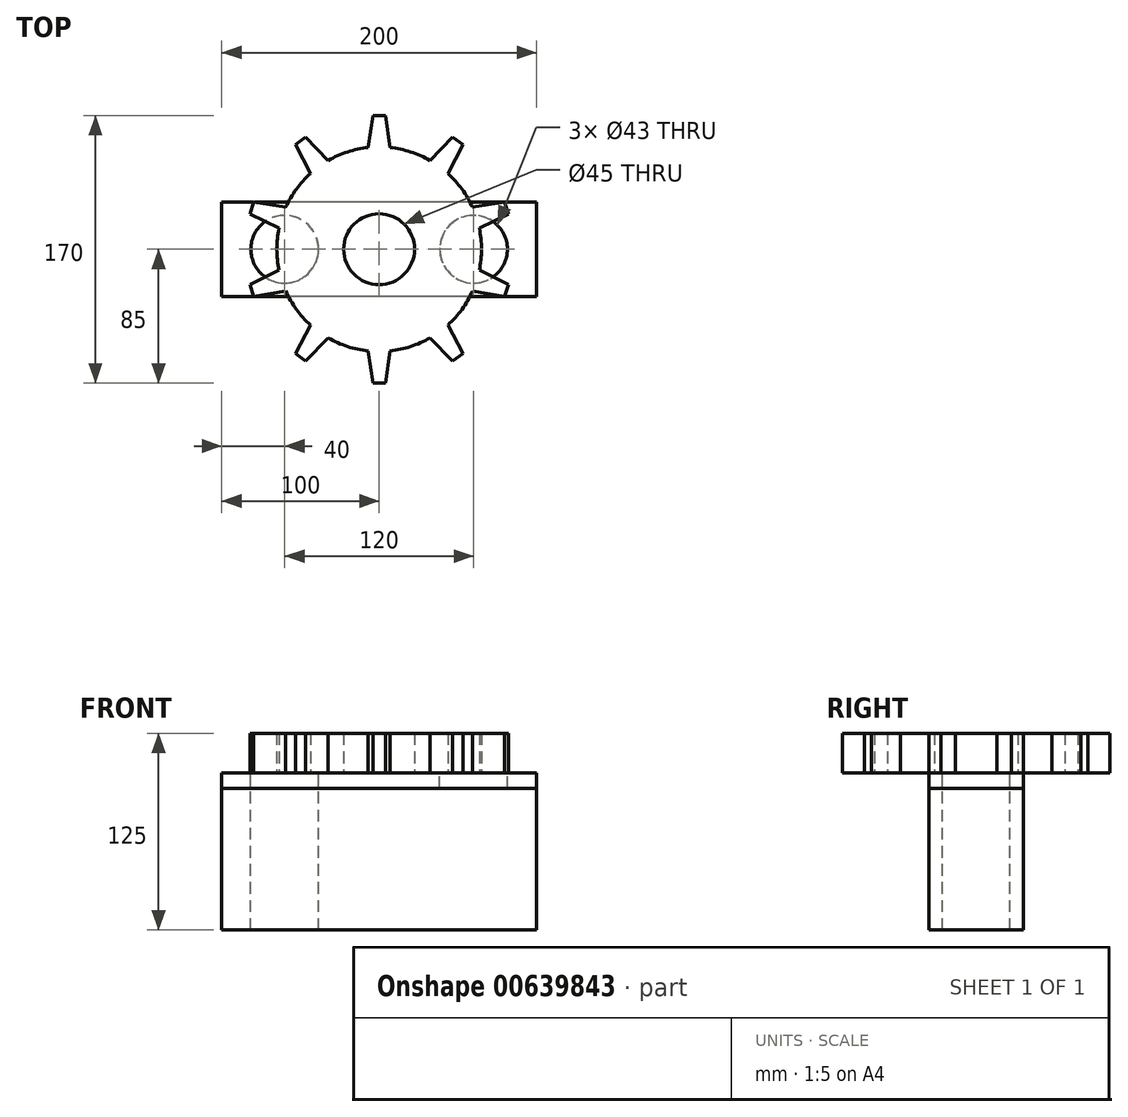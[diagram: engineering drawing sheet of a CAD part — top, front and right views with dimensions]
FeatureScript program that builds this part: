
annotation { "Feature Type Name" : "Feature", "Feature Type Description" : "" }
export const myFeature = defineFeature(function(context is Context, id is Id, definition is map)
    precondition{}
    {
        {
            var Q0;
            Q0=qCreatedBy(makeId("Top.planeOp"),FACE);
            var sketch = newSketch(context, id + "F0", { "sketchPlane" : qUnion([Q0])});
            skCircle(sketch, "E0", {"center": v(0, 0) * mm, "radius": 65 * mm});
            skLineSegment(sketch, "E1", {"start": v(0, 0) * mm, "end": v(0, 90) * mm, "construction": true});
            skLineSegment(sketch, "E2", {"start": v(0, 85) * mm, "end": v(-4, 85) * mm});
            skLineSegment(sketch, "E3", {"start": v(-4, 85) * mm, "end": v(-7, 64.62) * mm});
            skLineSegment(sketch, "E4.MirrorCS", {"start": v(0, 85) * mm, "end": v(4, 85) * mm});
            skLineSegment(sketch, "E5.MirrorCS", {"start": v(4, 85) * mm, "end": v(7, 64.62) * mm});
            skLineSegment(sketch, "E6.1.0", {"start": v(-49.96, 68.77) * mm, "end": v(-53.2, 66.42) * mm});
            skLineSegment(sketch, "E6.1.1", {"start": v(-49.96, 68.77) * mm, "end": v(-46.73, 71.12) * mm});
            skLineSegment(sketch, "E6.1.2", {"start": v(-46.73, 71.12) * mm, "end": v(-32.32, 56.4) * mm});
            skLineSegment(sketch, "E6.1.3", {"start": v(-53.2, 66.42) * mm, "end": v(-43.65, 48.17) * mm});
            skLineSegment(sketch, "E6.2.0", {"start": v(-80.84, 26.27) * mm, "end": v(-82.08, 22.46) * mm});
            skLineSegment(sketch, "E6.2.1", {"start": v(-80.84, 26.27) * mm, "end": v(-79.6, 30.07) * mm});
            skLineSegment(sketch, "E6.2.2", {"start": v(-79.6, 30.07) * mm, "end": v(-59.3, 26.63) * mm});
            skLineSegment(sketch, "E6.2.3", {"start": v(-82.08, 22.46) * mm, "end": v(-63.62, 13.31) * mm});
            skLineSegment(sketch, "E7.2.3.0", {"start": v(-80.84, -26.27) * mm, "end": v(-79.6, -30.07) * mm});
            skLineSegment(sketch, "E7.3.3.0", {"start": v(-80.84, -26.27) * mm, "end": v(-82.08, -22.46) * mm});
            skLineSegment(sketch, "E7.6.3.0", {"start": v(-82.08, -22.46) * mm, "end": v(-63.62, -13.31) * mm});
            skLineSegment(sketch, "E7.9.3.0", {"start": v(-79.6, -30.07) * mm, "end": v(-59.3, -26.63) * mm});
            skLineSegment(sketch, "E7.2.4.0", {"start": v(-49.96, -68.77) * mm, "end": v(-46.73, -71.12) * mm});
            skLineSegment(sketch, "E7.3.4.0", {"start": v(-49.96, -68.77) * mm, "end": v(-53.2, -66.42) * mm});
            skLineSegment(sketch, "E7.6.4.0", {"start": v(-53.2, -66.42) * mm, "end": v(-43.65, -48.17) * mm});
            skLineSegment(sketch, "E7.9.4.0", {"start": v(-46.73, -71.12) * mm, "end": v(-32.32, -56.4) * mm});
            skLineSegment(sketch, "E8.2.5.0", {"start": v(0, -85) * mm, "end": v(4, -85) * mm});
            skLineSegment(sketch, "E8.3.5.0", {"start": v(0, -85) * mm, "end": v(-4, -85) * mm});
            skLineSegment(sketch, "E8.6.5.0", {"start": v(-4, -85) * mm, "end": v(-7, -64.62) * mm});
            skLineSegment(sketch, "E8.9.5.0", {"start": v(4, -85) * mm, "end": v(7, -64.62) * mm});
            skLineSegment(sketch, "E8.2.6.0", {"start": v(49.96, -68.77) * mm, "end": v(53.2, -66.42) * mm});
            skLineSegment(sketch, "E8.3.6.0", {"start": v(49.96, -68.77) * mm, "end": v(46.73, -71.12) * mm});
            skLineSegment(sketch, "E8.6.6.0", {"start": v(46.73, -71.12) * mm, "end": v(32.32, -56.4) * mm});
            skLineSegment(sketch, "E8.9.6.0", {"start": v(53.2, -66.42) * mm, "end": v(43.65, -48.17) * mm});
            skLineSegment(sketch, "E8.2.7.0", {"start": v(80.84, -26.27) * mm, "end": v(82.08, -22.46) * mm});
            skLineSegment(sketch, "E8.3.7.0", {"start": v(80.84, -26.27) * mm, "end": v(79.6, -30.07) * mm});
            skLineSegment(sketch, "E8.6.7.0", {"start": v(79.6, -30.07) * mm, "end": v(59.3, -26.63) * mm});
            skLineSegment(sketch, "E8.9.7.0", {"start": v(82.08, -22.46) * mm, "end": v(63.62, -13.31) * mm});
            skLineSegment(sketch, "E8.2.8.0", {"start": v(80.84, 26.27) * mm, "end": v(79.6, 30.07) * mm});
            skLineSegment(sketch, "E8.3.8.0", {"start": v(80.84, 26.27) * mm, "end": v(82.08, 22.46) * mm});
            skLineSegment(sketch, "E8.6.8.0", {"start": v(82.08, 22.46) * mm, "end": v(63.62, 13.31) * mm});
            skLineSegment(sketch, "E8.9.8.0", {"start": v(79.6, 30.07) * mm, "end": v(59.3, 26.63) * mm});
            skLineSegment(sketch, "E8.2.9.0", {"start": v(49.96, 68.77) * mm, "end": v(46.73, 71.12) * mm});
            skLineSegment(sketch, "E8.3.9.0", {"start": v(49.96, 68.77) * mm, "end": v(53.2, 66.42) * mm});
            skLineSegment(sketch, "E8.6.9.0", {"start": v(53.2, 66.42) * mm, "end": v(43.65, 48.17) * mm});
            skLineSegment(sketch, "E8.9.9.0", {"start": v(46.73, 71.12) * mm, "end": v(32.32, 56.4) * mm});
            skCircle(sketch, "E9", {"center": v(0, 0) * mm, "radius": 22.5 * mm});
            skSolve(sketch);
        }
        {
            var Q0;
            Q0=makeQuery(id+"F0.imprint","IMPRINT",FACE,{"disambiguationData":[TD([[makeQuery(id+"F0.imprint","IMPRINT",EDGE,{"derivedFrom":sQuery(id+"F0.wireOp",EDGE,"E9")}),-1.0]])]});
            var Q1;
            Q1=makeQuery(id+"F0.imprint","IMPRINT",FACE,{"disambiguationData":[TD([[makeQuery(id+"F0.imprint","IMPRINT",EDGE,{"derivedFrom":sQuery(id+"F0.wireOp",EDGE,"E8.2.6.0")}),1.0]])]});
            var Q2;
            Q2=makeQuery(id+"F0.imprint","IMPRINT",FACE,{"disambiguationData":[TD([[makeQuery(id+"F0.imprint","IMPRINT",EDGE,{"derivedFrom":sQuery(id+"F0.wireOp",EDGE,"E8.2.7.0")}),1.0]])]});
            var Q3;
            Q3=makeQuery(id+"F0.imprint","IMPRINT",FACE,{"disambiguationData":[TD([[makeQuery(id+"F0.imprint","IMPRINT",EDGE,{"derivedFrom":sQuery(id+"F0.wireOp",EDGE,"E8.2.8.0")}),1.0]])]});
            var Q4;
            Q4=makeQuery(id+"F0.imprint","IMPRINT",FACE,{"disambiguationData":[TD([[makeQuery(id+"F0.imprint","IMPRINT",EDGE,{"derivedFrom":sQuery(id+"F0.wireOp",EDGE,"E8.2.9.0")}),1.0]])]});
            var Q5;
            Q5=makeQuery(id+"F0.imprint","IMPRINT",FACE,{"disambiguationData":[TD([[makeQuery(id+"F0.imprint","IMPRINT",EDGE,{"derivedFrom":sQuery(id+"F0.wireOp",EDGE,"E2")}),1.0]])]});
            var Q6;
            Q6=makeQuery(id+"F0.imprint","IMPRINT",FACE,{"disambiguationData":[TD([[makeQuery(id+"F0.imprint","IMPRINT",EDGE,{"derivedFrom":sQuery(id+"F0.wireOp",EDGE,"E6.1.0")}),1.0]])]});
            var Q7;
            Q7=makeQuery(id+"F0.imprint","IMPRINT",FACE,{"disambiguationData":[TD([[makeQuery(id+"F0.imprint","IMPRINT",EDGE,{"derivedFrom":sQuery(id+"F0.wireOp",EDGE,"E6.2.0")}),1.0]])]});
            var Q8;
            Q8=makeQuery(id+"F0.imprint","IMPRINT",FACE,{"disambiguationData":[TD([[makeQuery(id+"F0.imprint","IMPRINT",EDGE,{"derivedFrom":sQuery(id+"F0.wireOp",EDGE,"E7.2.3.0")}),1.0]])]});
            var Q9;
            Q9=makeQuery(id+"F0.imprint","IMPRINT",FACE,{"disambiguationData":[TD([[makeQuery(id+"F0.imprint","IMPRINT",EDGE,{"derivedFrom":sQuery(id+"F0.wireOp",EDGE,"E7.2.4.0")}),1.0]])]});
            var Q10;
            Q10=makeQuery(id+"F0.imprint","IMPRINT",FACE,{"disambiguationData":[TD([[makeQuery(id+"F0.imprint","IMPRINT",EDGE,{"derivedFrom":sQuery(id+"F0.wireOp",EDGE,"E8.2.5.0")}),1.0]])]});
            extrude(context, id + "F1", {"entities" : qUnion([Q0, Q1, Q2, Q3, Q4, Q5, Q6, Q7, Q8, Q9, Q10]), "depth" : 25 * mm, "offsetDistance" : 25 * mm});
        }
        {
            var Q0;
            Q0=makeQuery(id+"F1.opExtrude","SWEPT_BODY",BODY,{"disambiguationData":[OSD([sQuery(id+"F0.wireOp",EDGE,"E0"),sQuery(id+"F0.wireOp",EDGE,"E2"),sQuery(id+"F0.wireOp",EDGE,"E3"),sQuery(id+"F0.wireOp",EDGE,"E4.MirrorCS"),sQuery(id+"F0.wireOp",EDGE,"E5.MirrorCS"),sQuery(id+"F0.wireOp",EDGE,"E6.1.0"),sQuery(id+"F0.wireOp",EDGE,"E6.1.1"),sQuery(id+"F0.wireOp",EDGE,"E6.1.2"),sQuery(id+"F0.wireOp",EDGE,"E6.1.3"),sQuery(id+"F0.wireOp",EDGE,"E6.2.0"),sQuery(id+"F0.wireOp",EDGE,"E6.2.1"),sQuery(id+"F0.wireOp",EDGE,"E6.2.2"),sQuery(id+"F0.wireOp",EDGE,"E6.2.3"),sQuery(id+"F0.wireOp",EDGE,"E7.2.3.0"),sQuery(id+"F0.wireOp",EDGE,"E7.3.3.0"),sQuery(id+"F0.wireOp",EDGE,"E7.6.3.0"),sQuery(id+"F0.wireOp",EDGE,"E7.9.3.0"),sQuery(id+"F0.wireOp",EDGE,"E7.2.4.0"),sQuery(id+"F0.wireOp",EDGE,"E7.3.4.0"),sQuery(id+"F0.wireOp",EDGE,"E7.6.4.0"),sQuery(id+"F0.wireOp",EDGE,"E7.9.4.0"),sQuery(id+"F0.wireOp",EDGE,"E8.2.5.0"),sQuery(id+"F0.wireOp",EDGE,"E8.3.5.0"),sQuery(id+"F0.wireOp",EDGE,"E8.6.5.0"),sQuery(id+"F0.wireOp",EDGE,"E8.9.5.0"),sQuery(id+"F0.wireOp",EDGE,"E8.2.6.0"),sQuery(id+"F0.wireOp",EDGE,"E8.3.6.0"),sQuery(id+"F0.wireOp",EDGE,"E8.6.6.0"),sQuery(id+"F0.wireOp",EDGE,"E8.9.6.0"),sQuery(id+"F0.wireOp",EDGE,"E8.2.7.0"),sQuery(id+"F0.wireOp",EDGE,"E8.3.7.0"),sQuery(id+"F0.wireOp",EDGE,"E8.6.7.0"),sQuery(id+"F0.wireOp",EDGE,"E8.9.7.0"),sQuery(id+"F0.wireOp",EDGE,"E8.2.8.0"),sQuery(id+"F0.wireOp",EDGE,"E8.3.8.0"),sQuery(id+"F0.wireOp",EDGE,"E8.6.8.0"),sQuery(id+"F0.wireOp",EDGE,"E8.9.8.0"),sQuery(id+"F0.wireOp",EDGE,"E8.2.9.0"),sQuery(id+"F0.wireOp",EDGE,"E8.3.9.0"),sQuery(id+"F0.wireOp",EDGE,"E8.6.9.0"),sQuery(id+"F0.wireOp",EDGE,"E8.9.9.0"),sQuery(id+"F0.wireOp",EDGE,"E9")])]});
            transform(context, id + "F2", {"entities" : qUnion([Q0]), "transformType" : TransformType.TRANSLATION_3D, "dx" : 0 * mm, "dy" : 0 * mm, "dz" : 0 * mm, "makeCopy" : true});
        }
        {
            var Q0;
            Q0=makeQuery(id+"F2.opPattern","COPY",BODY,{"derivedFrom":makeQuery(id+"F1.opExtrude","SWEPT_BODY",BODY,{"disambiguationData":[OSD([sQuery(id+"F0.wireOp",EDGE,"E0"),sQuery(id+"F0.wireOp",EDGE,"E2"),sQuery(id+"F0.wireOp",EDGE,"E3"),sQuery(id+"F0.wireOp",EDGE,"E4.MirrorCS"),sQuery(id+"F0.wireOp",EDGE,"E5.MirrorCS"),sQuery(id+"F0.wireOp",EDGE,"E6.1.0"),sQuery(id+"F0.wireOp",EDGE,"E6.1.1"),sQuery(id+"F0.wireOp",EDGE,"E6.1.2"),sQuery(id+"F0.wireOp",EDGE,"E6.1.3"),sQuery(id+"F0.wireOp",EDGE,"E6.2.0"),sQuery(id+"F0.wireOp",EDGE,"E6.2.1"),sQuery(id+"F0.wireOp",EDGE,"E6.2.2"),sQuery(id+"F0.wireOp",EDGE,"E6.2.3"),sQuery(id+"F0.wireOp",EDGE,"E7.2.3.0"),sQuery(id+"F0.wireOp",EDGE,"E7.3.3.0"),sQuery(id+"F0.wireOp",EDGE,"E7.6.3.0"),sQuery(id+"F0.wireOp",EDGE,"E7.9.3.0"),sQuery(id+"F0.wireOp",EDGE,"E7.2.4.0"),sQuery(id+"F0.wireOp",EDGE,"E7.3.4.0"),sQuery(id+"F0.wireOp",EDGE,"E7.6.4.0"),sQuery(id+"F0.wireOp",EDGE,"E7.9.4.0"),sQuery(id+"F0.wireOp",EDGE,"E8.2.5.0"),sQuery(id+"F0.wireOp",EDGE,"E8.3.5.0"),sQuery(id+"F0.wireOp",EDGE,"E8.6.5.0"),sQuery(id+"F0.wireOp",EDGE,"E8.9.5.0"),sQuery(id+"F0.wireOp",EDGE,"E8.2.6.0"),sQuery(id+"F0.wireOp",EDGE,"E8.3.6.0"),sQuery(id+"F0.wireOp",EDGE,"E8.6.6.0"),sQuery(id+"F0.wireOp",EDGE,"E8.9.6.0"),sQuery(id+"F0.wireOp",EDGE,"E8.2.7.0"),sQuery(id+"F0.wireOp",EDGE,"E8.3.7.0"),sQuery(id+"F0.wireOp",EDGE,"E8.6.7.0"),sQuery(id+"F0.wireOp",EDGE,"E8.9.7.0"),sQuery(id+"F0.wireOp",EDGE,"E8.2.8.0"),sQuery(id+"F0.wireOp",EDGE,"E8.3.8.0"),sQuery(id+"F0.wireOp",EDGE,"E8.6.8.0"),sQuery(id+"F0.wireOp",EDGE,"E8.9.8.0"),sQuery(id+"F0.wireOp",EDGE,"E8.2.9.0"),sQuery(id+"F0.wireOp",EDGE,"E8.3.9.0"),sQuery(id+"F0.wireOp",EDGE,"E8.6.9.0"),sQuery(id+"F0.wireOp",EDGE,"E8.9.9.0"),sQuery(id+"F0.wireOp",EDGE,"E9")])]}),"instanceName":"1"});
            deleteBodies(context, id + "F3", {"entities" : qUnion([Q0])});
        }
        {
            var Q0;
            Q0=qCreatedBy(makeId("Top.planeOp"),FACE);
            var sketch = newSketch(context, id + "F4", { "sketchPlane" : qUnion([Q0])});
            skLineSegment(sketch, "E10.bottom", {"start": v(100, -30) * mm, "end": v(-100, -30) * mm});
            skLineSegment(sketch, "E10.top", {"start": v(100, 30) * mm, "end": v(-100, 30) * mm});
            skLineSegment(sketch, "E10.left", {"start": v(100, -30) * mm, "end": v(100, 30) * mm});
            skLineSegment(sketch, "E10.right", {"start": v(-100, -30) * mm, "end": v(-100, 30) * mm});
            skPoint(sketch, "E10.middle", {"position": v(0, 0) * mm});
            skLineSegment(sketch, "E11", {"start": v(100, 0) * mm, "end": v(-100, 0) * mm, "construction": true});
            skCircle(sketch, "E12", {"center": v(60, 0) * mm, "radius": 21.5 * mm});
            skLineSegment(sketch, "E13", {"start": v(0, 0) * mm, "end": v(0, 30) * mm, "construction": true});
            skCircle(sketch, "E14.MirrorC", {"center": v(-60, 0) * mm, "radius": 21.5 * mm});
            skSolve(sketch);
        }
        {
            var Q0;
            Q0=makeQuery(id+"F4.imprint","IMPRINT",FACE,{"disambiguationData":[TD([[makeQuery(id+"F4.imprint","IMPRINT",EDGE,{"derivedFrom":sQuery(id+"F4.wireOp",EDGE,"E14.MirrorC")}),-1.0]])]});
            var Q1;
            Q1=makeQuery(id+"F4.imprint","IMPRINT",FACE,{"disambiguationData":[TD([[makeQuery(id+"F4.imprint","IMPRINT",EDGE,{"derivedFrom":sQuery(id+"F4.wireOp",EDGE,"E12")}),1.0]])]});
            extrude(context, id + "F5", {"entities" : qUnion([Q0, Q1]), "oppositeDirection" : true, "depth" : 100 * mm, "offsetDistance" : 25 * mm});
        }
        {
            var Q0;
            Q0 = qSketchRegion(id + "F4", true);
            extrude(context, id + "F6", {"entities" : qUnion([Q0]), "oppositeDirection" : true, "depth" : 10 * mm, "offsetDistance" : 25 * mm});
        }
    });
